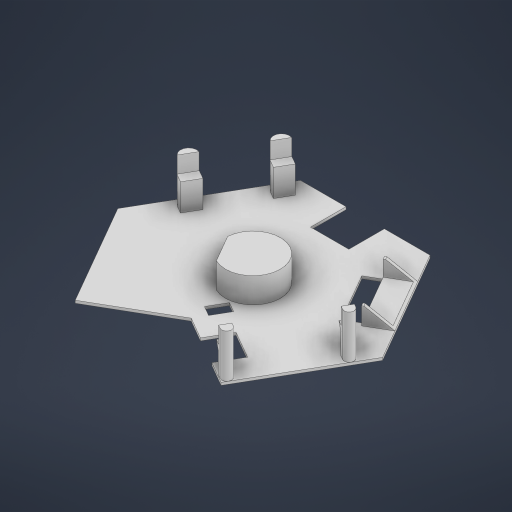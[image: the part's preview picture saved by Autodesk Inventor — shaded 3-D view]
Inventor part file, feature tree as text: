
AUTODESK INVENTOR PART (.ipt)
format: ipt  version: 2023 (Build 270158000, 158)  size: 530,432 bytes
history: native  units: in
note: dims shown in document units (in); Inventor stores cm internally (conversion verified against a paired STEP export)
features: extrude x13, sketch x8, move_body x7, direct_edit x6, chamfer x4
ambient origin geometry x8: Origin, YZ Plane, XZ Plane, XY Plane, X Axis, Y Axis, Z Axis, Center Point
bodies: Solid1 (feature_tree)
feature tree (38):
  sketch  "Sketch1"  dims[d0=2.5394in d1=0.1287in]
  extrude  "Extrusion1"  Depth=2.5394in
  extrude  "Extrusion2"  Depth=0.0394in
  extrude  "Extrusion3"  Depth=0.0492in TaperAngle=0.0deg
  extrude  "Extrusion4"  Depth=0.2756in TaperAngle=0.0deg
  sketch  "Sketch3"  dims[d4=0.0394in d5=0.0492in d6=0.0in]
  extrude  "Extrusion5"  Depth=1.0531in TaperAngle=0.0deg
  extrude  "Extrusion6"  Depth=0.315in
  extrude  "Extrusion7"  Depth=0.4528in
  extrude  "Extrusion8"  Depth=0.4016in
  chamfer  "Chamfer1"  Distance=0.2953in
  chamfer  "Chamfer2"  Distance=0.1772in
  direct_edit  "Direct Edit1"
  extrude  "Extrusion9"  Depth=0.1772in
  direct_edit  "Direct Edit2"
  direct_edit  "Direct Edit3"
  direct_edit  "Direct Edit4"
  direct_edit  "Direct Edit5"
  sketch  "Sketch7"  dims[d16=0.4528in d17=0.2165in]
  extrude  "Extrusion10"  Depth=0.3937in
  chamfer  "Chamfer3"  Distance=0.189in
  chamfer  "Chamfer4"  Distance=0.5827in
  extrude  "Extrusion11"  Depth=0.0197in
  extrude  "Extrusion12"  Depth=0.0492in
  direct_edit  "Direct Edit6"
  extrude  "Extrusion13"  Depth=0.0197in
  sketch  "Sketch2"  dims[d2=0.0394in d3=0.5413in]
  sketch  "Sketch4"  dims[d7=0.315in d8=0.0in d9=0.2756in d10=0.0in]
  sketch  "Sketch5"  dims[d11=1.0531in d12=0.2165in d13=0.0in]
  sketch  "Sketch6"  dims[d14=0.315in d15=0.315in]
  sketch  "Sketch8"  dims[d18=0.2165in d19=0.4016in d20=0.2953in d21=0.1772in d22=0.1772in d23=0.3937in d24=0.189in d25=0.5827in d26=0.7008in d27=0.0492in d29=0.9449in d30=0.8346in d31=0.6299in d32=0.0492in d33=0.0492in d34=0.31in d35=0.0492in d36=1.1122in d38=0.689in d39=0.0394in d40=0.0394in d41=0.0394in d42=0.0787in d43=0.0in d44=0.1083in d45=0.0in d46=0.0844in d47=0.1945in d48=0.1969in d49=0.1811in d50=0.4626in d51=0.1937in d52=0.1969in d53=0.185in d54=0.1339in d55=0.1185in d56=0.1063in d57=0.0059in d58=0.1205in d59=0.1228in d60=0.1102in d61=0.1949in d62=0.1201in d63=0.1339in d64=0.1102in d65=0.3543in d66=0.0in d67=0.1654in d68=0.1654in d69=0.0079in d70=0.0in d71=0.126in d72=0.1102in d73=45.0deg d74=0.126in d75=0.1102in d76=45.0deg d77=0.0in d78=0.0in d79=-0.0039in d80=0.0in d81=0.0in d82=-0.0039in d83=0.0984in d84=0.0984in d85=0.0984in d86=0.0984in d87=0.1181in d88=0.0in d89=0.0in d90=0.0in d91=-0.0689in d92=0.0in d93=0.0in d94=-0.0236in d95=0.0in d96=0.0in d97=-0.0689in d98=0.0in d99=0.0in d100=-0.0197in d101=0.0394in d102=0.2756in d103=0.1969in d104=0.0in d105=0.2559in d106=0.1969in d107=45.0deg d108=0.2559in d109=0.1969in d110=45.0deg d111=0.1969in d112=0.0in d113=0.0197in d114=0.0in d115=0.0in d116=0.0in d117=-0.875in d118=0.3504in d119=0.128in d120=0.2067in d121=0.0in d122=0.0in d123=0.0197in d124=0.0344in d125=0.0197in d126=0.0344in]
  move_body  "Move1"
  move_body  "Move2"
  move_body  "Move3"
  move_body  "Move4"
  move_body  "Move5"
  move_body  "Move6"
  move_body  "Move7"
